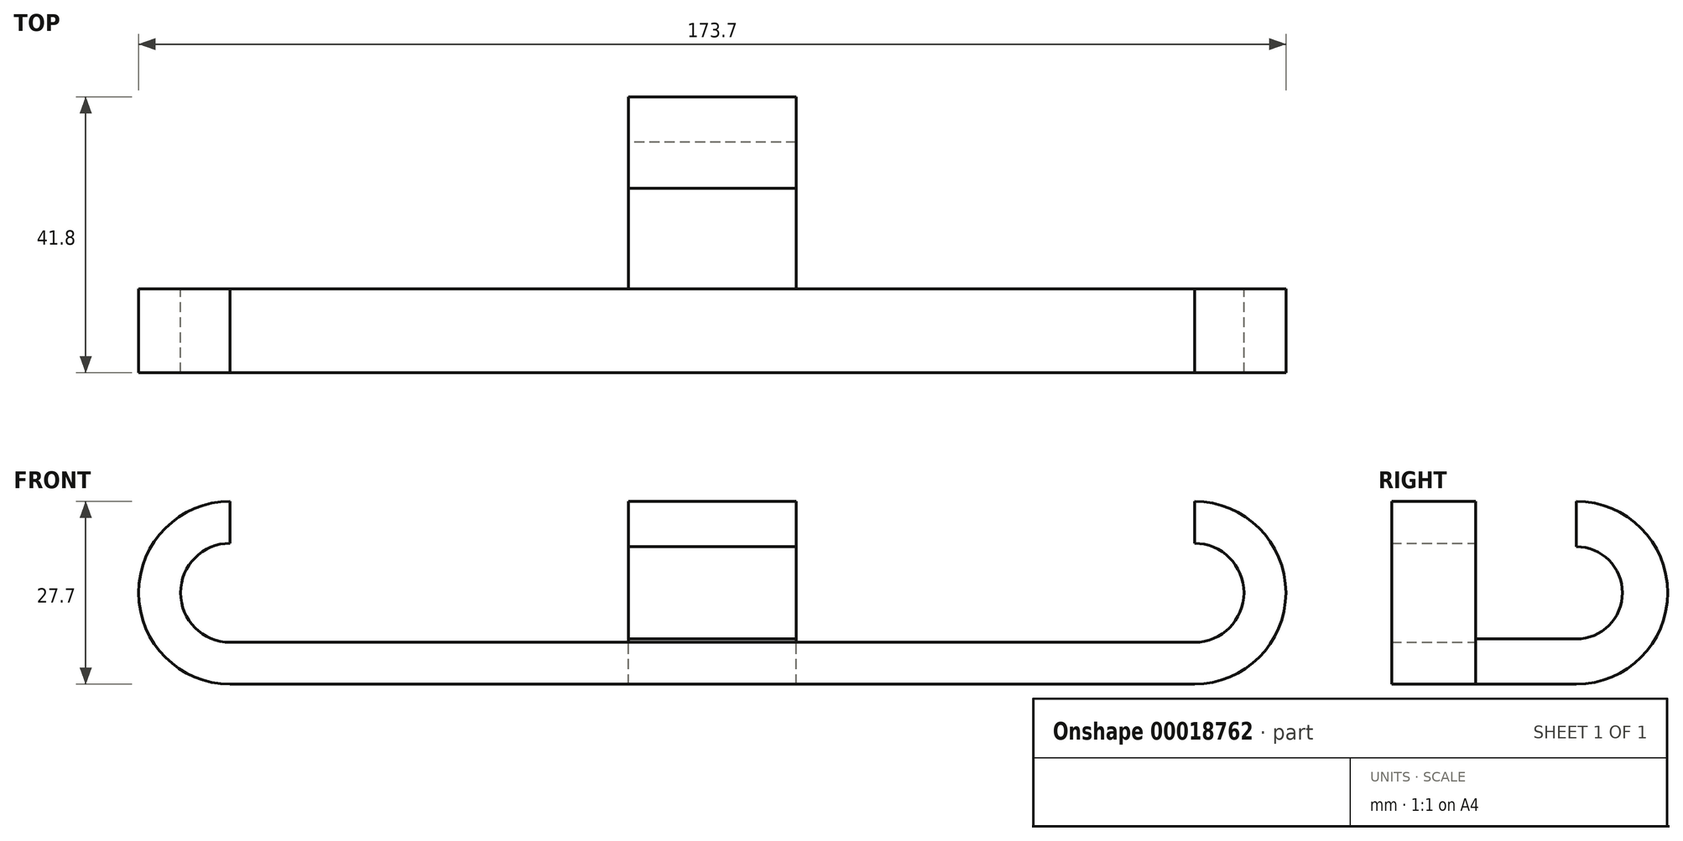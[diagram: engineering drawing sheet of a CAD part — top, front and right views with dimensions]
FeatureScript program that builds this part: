
annotation { "Feature Type Name" : "Feature", "Feature Type Description" : "" }
export const myFeature = defineFeature(function(context is Context, id is Id, definition is map)
    precondition{}
    {
        {
            var Q0;
            Q0=qCreatedBy(makeId("Front.planeOp"),FACE);
            var sketch = newSketch(context, id + "F0", { "sketchPlane" : qUnion([Q0])});
            skLineSegment(sketch, "E0", {"start": v(0, -27.7) * mm, "end": v(-73, -27.7) * mm});
            skArc(sketch, "E1", {"start": v(-73, 0) * mm, "mid": v(-86.85, -13.85) * mm, "end": v(-73, -27.7) * mm});
            skLineSegment(sketch, "E2", {"start": v(0, -21.35) * mm, "end": v(-73, -21.35) * mm});
            skArc(sketch, "E3", {"start": v(-73, -6.35) * mm, "mid": v(-80.5, -13.85) * mm, "end": v(-73, -21.35) * mm});
            skLineSegment(sketch, "E4", {"start": v(-73, -6.35) * mm, "end": v(-73, 0) * mm});
            skLineSegment(sketch, "E5.MirrorCS", {"start": v(0, -21.35) * mm, "end": v(73, -21.35) * mm});
            skLineSegment(sketch, "E6.MirrorCS", {"start": v(73, -6.35) * mm, "end": v(73, 0) * mm});
            skArc(sketch, "E7.MirrorCS", {"start": v(73, 0) * mm, "mid": v(86.85, -13.85) * mm, "end": v(73, -27.7) * mm});
            skArc(sketch, "E8.MirrorCS", {"start": v(73, -6.35) * mm, "mid": v(80.5, -13.85) * mm, "end": v(73, -21.35) * mm});
            skLineSegment(sketch, "E9.MirrorCS", {"start": v(0, -27.7) * mm, "end": v(73, -27.7) * mm});
            skLineSegment(sketch, "E10", {"start": v(-80.5, -13.85) * mm, "end": v(80.5, -13.85) * mm, "construction": true});
            skLineSegment(sketch, "E11", {"start": v(-73, -21.35) * mm, "end": v(-73, -6.35) * mm, "construction": true});
            skSolve(sketch);
        }
        {
            var Q0;
            Q0=makeQuery(id+"F0.imprint","IMPRINT",FACE,{"disambiguationData":[TD([[makeQuery(id+"F0.imprint","IMPRINT",EDGE,{"derivedFrom":sQuery(id+"F0.wireOp",EDGE,"E0")}),-1.0]])]});
            extrude(context, id + "F1", {"entities" : qUnion([Q0]), "depth" : 12.7 * mm});
        }
        {
            var Q0;
            Q0=qCreatedBy(makeId("Right.planeOp"),FACE);
            var sketch = newSketch(context, id + "F2", { "sketchPlane" : qUnion([Q0])});
            skLineSegment(sketch, "E12.0.0", {"start": v(0, -27.7) * mm, "end": v(0, 0) * mm});
            skLineSegment(sketch, "E12.0.1", {"start": v(0, 0) * mm, "end": v(-12.7, 0) * mm});
            skLineSegment(sketch, "E12.0.2", {"start": v(-12.7, 0) * mm, "end": v(-12.7, -27.7) * mm});
            skLineSegment(sketch, "E12.0.3", {"start": v(-12.7, -27.7) * mm, "end": v(0, -27.7) * mm});
            skLineSegment(sketch, "E13", {"start": v(-12.7, -5.5) * mm, "end": v(-12.7, 0) * mm});
            skLineSegment(sketch, "E14", {"start": v(0, -27.7) * mm, "end": v(15.25, -27.7) * mm});
            skLineSegment(sketch, "E15", {"start": v(-43.18, -13.85) * mm, "end": v(71.82, -13.85) * mm, "construction": true});
            skArc(sketch, "E16", {"start": v(15.25, -27.7) * mm, "mid": v(29.1, -13.85) * mm, "end": v(15.25, 0) * mm});
            skLineSegment(sketch, "E17", {"start": v(0, -20.85) * mm, "end": v(15.25, -20.85) * mm});
            skLineSegment(sketch, "E18.MirrorCS", {"start": v(0, -6.85) * mm, "end": v(15.25, -6.85) * mm, "construction": true});
            skArc(sketch, "E19", {"start": v(15.25, -20.85) * mm, "mid": v(22.25, -13.85) * mm, "end": v(15.25, -6.85) * mm});
            skLineSegment(sketch, "E20", {"start": v(15.25, 0) * mm, "end": v(15.25, -6.85) * mm});
            skLineSegment(sketch, "E21", {"start": v(15.25, -20.85) * mm, "end": v(15.25, -6.85) * mm, "construction": true});
            skSolve(sketch);
        }
        {
            var Q0;
            {var subQ1=sQuery(id+"F2.wireOp",EDGE,"E14");Q0=makeQuery(id+"F2.imprint","IMPRINT",FACE,{"disambiguationData":[TD([[makeQuery(id+"F2.imprint","IMPRINT",EDGE,{"derivedFrom":subQ1}),1.0]])]});}
            extrude(context, id + "F3", {"entities" : qUnion([Q0]), "operationType" : NewBodyOperationType.ADD, "endBound" : BoundingType.SYMMETRIC, "depth" : 25.4 * mm});
        }
    });
